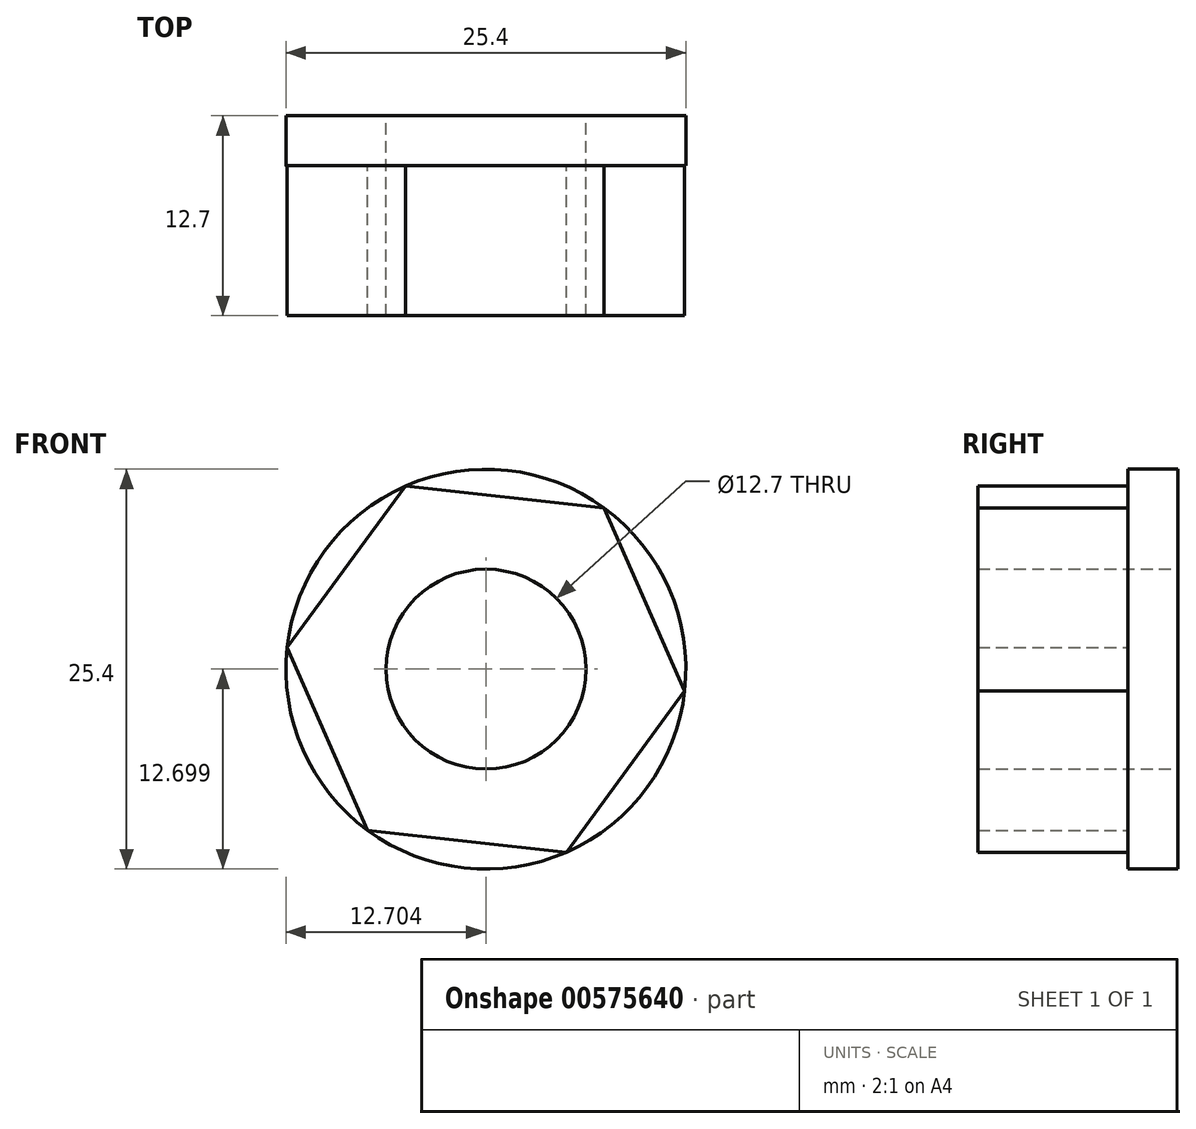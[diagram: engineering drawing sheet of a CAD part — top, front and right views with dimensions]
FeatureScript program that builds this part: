
annotation { "Feature Type Name" : "Feature", "Feature Type Description" : "" }
export const myFeature = defineFeature(function(context is Context, id is Id, definition is map)
    precondition{}
    {
        {
            var Q0;
            Q0=qCreatedBy(makeId("Front.planeOp"),FACE);
            var sketch = newSketch(context, id + "F0", { "sketchPlane" : qUnion([Q0])});
            skCircle(sketch, "E0", {"center": v(-49.28, 2.03) * mm, "radius": 6.35 * mm});
            skCircle(sketch, "E1.0", {"center": v(-49.28, 2.03) * mm, "radius": 12.7 * mm});
            skSolve(sketch);
        }
        {
            var Q0;
            Q0=qSketchRegion(id+"F0",true);
            extrude(context, id + "F1", {"entities" : qUnion([Q0]), "depth" : 3.17 * mm, "offsetDistance" : 25.4 * mm});
        }
        {
            var Q0;
            Q0=makeQuery(id+"F1.opExtrude","CAP_FACE",FACE,{"disambiguationData":[OSD([sQuery(id+"F0.wireOp",EDGE,"E0"),sQuery(id+"F0.wireOp",EDGE,"E1.0")])],"isStart":false});
            var sketch = newSketch(context, id + "F2", { "sketchPlane" : qUnion([Q0])});
            skCircle(sketch, "E2", {"center": v(-49.28, 2.03) * mm, "radius": 12.7 * mm});
            skCircle(sketch, "E3.cCircle", {"center": v(-49.28, 2.03) * mm, "radius": 12.7 * mm, "construction": true});
            skLineSegment(sketch, "E3.0", {"start": v(-36.65, 0.65) * mm, "end": v(-44.16, -9.6) * mm});
            skLineSegment(sketch, "E3.1", {"start": v(-44.16, -9.6) * mm, "end": v(-56.78, -8.21) * mm});
            skLineSegment(sketch, "E3.2", {"start": v(-56.78, -8.21) * mm, "end": v(-61.9, 3.4) * mm});
            skLineSegment(sketch, "E3.3", {"start": v(-61.9, 3.4) * mm, "end": v(-54.4, 13.65) * mm});
            skLineSegment(sketch, "E3.4", {"start": v(-54.4, 13.65) * mm, "end": v(-41.77, 12.27) * mm});
            skLineSegment(sketch, "E3.5", {"start": v(-41.77, 12.27) * mm, "end": v(-36.65, 0.65) * mm});
            skSolve(sketch);
        }
        {
            var Q0;
            Q0=makeQuery(id+"F2.imprint","IMPRINT",FACE,{"disambiguationData":[TD([[makeQuery(id+"F2.imprint","IMPRINT",EDGE,{"derivedFrom":sQuery(id+"F2.wireOp",EDGE,"E3.0")}),-1.0]])]});
            extrude(context, id + "F3", {"entities" : qUnion([Q0]), "operationType" : NewBodyOperationType.ADD, "depth" : 9.52 * mm, "offsetDistance" : 25.4 * mm});
        }
    });
